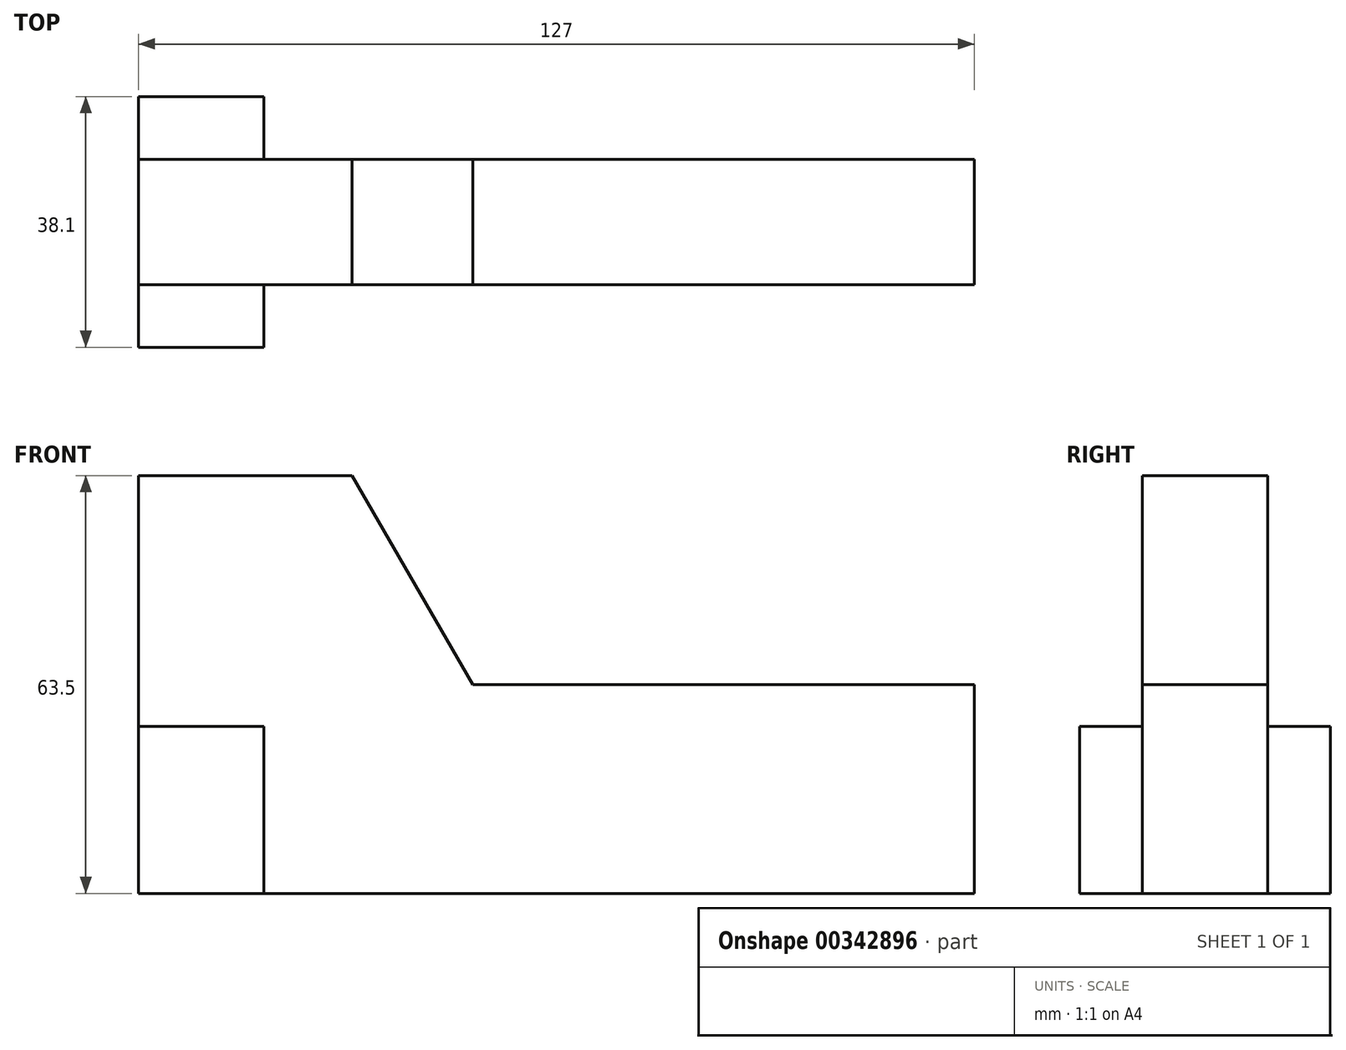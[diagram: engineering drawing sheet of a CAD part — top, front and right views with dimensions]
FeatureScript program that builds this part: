
annotation { "Feature Type Name" : "Feature", "Feature Type Description" : "" }
export const myFeature = defineFeature(function(context is Context, id is Id, definition is map)
    precondition{}
    {
        {
            var Q0;
            Q0=qCreatedBy(makeId("Front.planeOp"),FACE);
            var sketch = newSketch(context, id + "F0", { "sketchPlane" : qUnion([Q0])});
            skLineSegment(sketch, "E0", {"start": v(-56.5, 31.17) * mm, "end": v(-56.5, -32.33) * mm});
            skLineSegment(sketch, "E1", {"start": v(-56.5, -32.33) * mm, "end": v(70.5, -32.33) * mm});
            skLineSegment(sketch, "E2", {"start": v(70.5, -32.33) * mm, "end": v(70.5, -0.58) * mm});
            skLineSegment(sketch, "E3", {"start": v(70.5, -0.58) * mm, "end": v(-5.7, -0.58) * mm});
            skLineSegment(sketch, "E4", {"start": v(-5.7, -0.58) * mm, "end": v(-24.03, 31.17) * mm});
            skLineSegment(sketch, "E5", {"start": v(-24.03, 31.17) * mm, "end": v(-56.5, 31.17) * mm});
            skSolve(sketch);
        }
        {
            var Q0;
            Q0=makeQuery(id+"F0.imprint","IMPRINT",FACE,{"disambiguationData":[TD([[makeQuery(id+"F0.imprint","IMPRINT",EDGE,{"derivedFrom":sQuery(id+"F0.wireOp",EDGE,"E0")}),1.0]])]});
            extrude(context, id + "F1", {"entities" : qUnion([Q0]), "depth" : 19.05 * mm});
        }
        {
            var Q0;
            Q0=makeQuery(id+"F1.opExtrude","CAP_FACE",FACE,{"disambiguationData":[OSD([sQuery(id+"F0.wireOp",EDGE,"E0"),sQuery(id+"F0.wireOp",EDGE,"E1"),sQuery(id+"F0.wireOp",EDGE,"E2"),sQuery(id+"F0.wireOp",EDGE,"E3"),sQuery(id+"F0.wireOp",EDGE,"E4"),sQuery(id+"F0.wireOp",EDGE,"E5")])],"isStart":false});
            var sketch = newSketch(context, id + "F2", { "sketchPlane" : qUnion([Q0])});
            skLineSegment(sketch, "E6.bottom", {"start": v(-56.5, -32.33) * mm, "end": v(-37.45, -32.33) * mm});
            skLineSegment(sketch, "E6.top", {"start": v(-56.5, -6.93) * mm, "end": v(-37.45, -6.93) * mm});
            skLineSegment(sketch, "E6.left", {"start": v(-56.5, -32.33) * mm, "end": v(-56.5, -6.93) * mm});
            skLineSegment(sketch, "E6.right", {"start": v(-37.45, -32.33) * mm, "end": v(-37.45, -6.93) * mm});
            skSolve(sketch);
        }
        {
            var Q0;
            Q0 = qSketchRegion(id + "F2", true);
            extrude(context, id + "F3", {"entities" : qUnion([Q0]), "operationType" : NewBodyOperationType.ADD, "depth" : 9.52 * mm});
        }
        {
            var Q0;
            Q0=makeQuery(id+"F1.opExtrude","CAP_FACE",FACE,{"disambiguationData":[OSD([sQuery(id+"F0.wireOp",EDGE,"E0"),sQuery(id+"F0.wireOp",EDGE,"E1"),sQuery(id+"F0.wireOp",EDGE,"E2"),sQuery(id+"F0.wireOp",EDGE,"E3"),sQuery(id+"F0.wireOp",EDGE,"E4"),sQuery(id+"F0.wireOp",EDGE,"E5")])],"isStart":true});
            var sketch = newSketch(context, id + "F4", { "sketchPlane" : qUnion([Q0])});
            skLineSegment(sketch, "E7.bottom", {"start": v(56.5, -32.33) * mm, "end": v(37.45, -32.33) * mm});
            skLineSegment(sketch, "E7.top", {"start": v(56.5, -6.93) * mm, "end": v(37.45, -6.93) * mm});
            skLineSegment(sketch, "E7.left", {"start": v(56.5, -32.33) * mm, "end": v(56.5, -6.93) * mm});
            skLineSegment(sketch, "E7.right", {"start": v(37.45, -32.33) * mm, "end": v(37.45, -6.93) * mm});
            skSolve(sketch);
        }
        {
            var Q0;
            Q0=makeQuery(id+"F4.imprint","IMPRINT",FACE,{"disambiguationData":[TD([[makeQuery(id+"F4.imprint","IMPRINT",EDGE,{"derivedFrom":sQuery(id+"F4.wireOp",EDGE,"E7.bottom")}),-1.0]])]});
            extrude(context, id + "F5", {"entities" : qUnion([Q0]), "operationType" : NewBodyOperationType.ADD, "depth" : 9.52 * mm});
        }
    });
